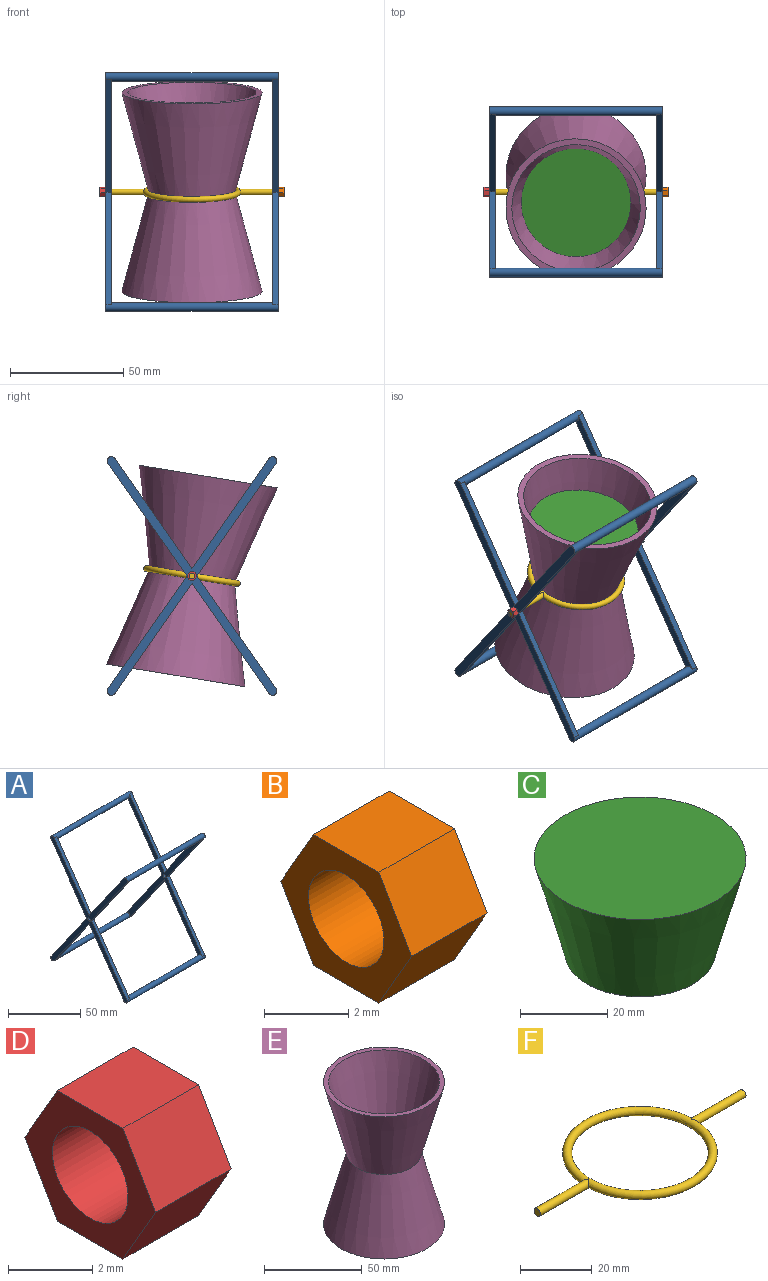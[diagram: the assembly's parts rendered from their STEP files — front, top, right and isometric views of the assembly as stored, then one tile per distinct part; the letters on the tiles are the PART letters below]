
ASSEMBLY  parts=6 mates=5
PART A: 26 faces, bbox 76.2x75x105.4 mm
  f0: cylinder r=1.91mm len=76.2mm, axis (-1,0,0), area 881.7mm2, adj f1,f11,f13,f14,f15,f16,f23,f25
  f1: plane 49.71x34.81mm, normal (0,-0.82,-0.57), area 154.1mm2, adj f0,f2,f13,f14
  f2: plane 49.71x34.81mm, normal (0,-0.82,0.57), area 154.1mm2, adj f1,f3,f13,f14
  f3: cylinder r=1.91mm len=76.2mm, axis (-1,0,0), area 881.7mm2, adj f2,f4,f13,f14,f15,f17,f18,f25
  f4: plane 48.57x34.01mm, normal (0,0.82,-0.57), area 150.6mm2, adj f3,f5,f13,f14
  f5: plane 48.57x34.01mm, normal (0,-0.82,-0.57), area 150.6mm2, adj f4,f6,f13,f14
  f6: cylinder r=1.91mm len=76.2mm, axis (-1,0,0), area 881.7mm2, adj f5,f7,f13,f14,f15,f19,f20,f25
  f7: plane 49.71x34.81mm, normal (0,0.82,0.57), area 154.1mm2, adj f6,f8,f13,f14
  f8: plane 49.71x34.81mm, normal (0,0.82,-0.57), area 154.1mm2, adj f7,f9,f13,f14
  f9: cylinder r=1.91mm len=76.2mm, axis (-1,0,0), area 881.7mm2, adj f8,f10,f13,f14,f15,f21,f22,f25
  f10: plane 48.57x34.01mm, normal (0,-0.82,0.57), area 150.6mm2, adj f9,f11,f13,f14
  f11: plane 48.57x34.01mm, normal (0,0.82,0.57), area 150.6mm2, adj f0,f10,f13,f14
  f12: cylinder r=1.27mm len=2.54mm, axis (-1,0,0), area 20.3mm2, adj f13,f14
  f13: plane 105.41x74.95mm, normal (1,0,0), area 947.4mm2, adj f0,f1,f2,f3,f4,f5,f6,f7
  f14: plane 103.79x74.26mm, normal (-1,0,0), area 901.8mm2, adj f0,f1,f2,f3,f4,f5,f6,f7
  f15: plane 103.79x74.26mm, normal (1,0,0), area 901.8mm2, adj f0,f3,f6,f9,f16,f17,f18,f19
  f16: plane 49.71x34.81mm, normal (0,-0.82,-0.57), area 154.1mm2, adj f0,f15,f17,f25
  f17: plane 49.71x34.81mm, normal (0,-0.82,0.57), area 154.1mm2, adj f3,f15,f16,f25
  f18: plane 48.57x34.01mm, normal (0,0.82,-0.57), area 150.6mm2, adj f3,f15,f19,f25
  f19: plane 48.57x34.01mm, normal (0,-0.82,-0.57), area 150.6mm2, adj f6,f15,f18,f25
  f20: plane 49.71x34.81mm, normal (0,0.82,0.57), area 154.1mm2, adj f6,f15,f21,f25
  f21: plane 49.71x34.81mm, normal (0,0.82,-0.57), area 154.1mm2, adj f9,f15,f20,f25
  f22: plane 48.57x34.01mm, normal (0,-0.82,0.57), area 150.6mm2, adj f9,f15,f23,f25
  f23: plane 48.57x34.01mm, normal (0,0.82,0.57), area 150.6mm2, adj f0,f15,f22,f25
  f24: cylinder r=1.27mm len=2.54mm, axis (1,0,0), area 20.3mm2, adj f15,f25
  f25: plane 105.41x74.95mm, normal (-1,0,0), area 947.4mm2, adj f0,f3,f6,f9,f16,f17,f18,f19
PART B: 9 faces, bbox 2.5x4.4x3.8 mm
  f0: plane 2.54x1.91mm, normal (0,0.87,0.5), area 5.6mm2, adj f1,f6,f7,f8
  f1: plane 2.54x2.2mm, normal (0,0,1), area 5.6mm2, adj f0,f2,f7,f8
  f2: plane 2.54x1.91mm, normal (0,-0.87,0.5), area 5.6mm2, adj f1,f3,f7,f8
  f3: plane 2.54x1.91mm, normal (0,-0.87,-0.5), area 5.6mm2, adj f2,f4,f7,f8
  f4: plane 2.54x2.2mm, normal (0,0,-1), area 5.6mm2, adj f3,f6,f7,f8
  f5: cylinder r=1.27mm len=2.54mm, axis (-1,0,0), area 20.3mm2, adj f7,f8
  f6: plane 2.54x1.91mm, normal (0,0.87,-0.5), area 5.6mm2, adj f0,f4,f7,f8
  f7: plane 4.4x3.81mm, normal (1,0,0), area 7.5mm2, adj f0,f1,f2,f3,f4,f5,f6
  f8: plane 4.4x3.81mm, normal (-1,0,0), area 7.5mm2, adj f0,f1,f2,f3,f4,f5,f6
PART C: 3 faces, bbox 48.6x48.6x26.7 mm
  f0: plane 48.57x48.57mm, normal (0,0,1), area 1853.1mm2, adj f1
  f1: cone r=24.29mm half-angle=15deg, axis (0,0,1), area 3600.6mm2, adj f0,f2
  f2: plane 34.25x34.25mm, normal (0,0,-1), area 921.2mm2, adj f1
PART D: 9 faces, bbox 2.5x4.4x3.8 mm
  f0: plane 2.54x1.91mm, normal (0,0.87,0.5), area 5.6mm2, adj f1,f6,f7,f8
  f1: plane 2.54x2.2mm, normal (0,0,1), area 5.6mm2, adj f0,f2,f7,f8
  f2: plane 2.54x1.91mm, normal (0,-0.87,0.5), area 5.6mm2, adj f1,f3,f7,f8
  f3: plane 2.54x1.91mm, normal (0,-0.87,-0.5), area 5.6mm2, adj f2,f4,f7,f8
  f4: plane 2.54x2.2mm, normal (0,0,-1), area 5.6mm2, adj f3,f6,f7,f8
  f5: cylinder r=1.27mm len=2.54mm, axis (1,0,0), area 20.3mm2, adj f7,f8
  f6: plane 2.54x1.91mm, normal (0,0.87,-0.5), area 5.6mm2, adj f0,f4,f7,f8
  f7: plane 4.4x3.81mm, normal (-1,0,0), area 7.5mm2, adj f0,f1,f2,f3,f4,f5,f6
  f8: plane 4.4x3.81mm, normal (1,0,0), area 7.5mm2, adj f0,f1,f2,f3,f4,f5,f6
PART E: 6 faces, bbox 61.9x61.9x88.9 mm
  f0: cone r=19.05mm half-angle=15deg, axis (0,0,-1), area 7230mm2, adj f1,f3
  f1: plane 61.92x61.92mm, normal (0,0,-1), area 489.8mm2, adj f0,f4
  f2: plane 61.92x61.92mm, normal (0,0,1), area 489.8mm2, adj f3,f5
  f3: cone r=19.05mm half-angle=15deg, axis (0,0,1), area 7230mm2, adj f0,f2
  f4: cone r=16.6mm half-angle=15deg, axis (0,0,-1), area 6469.7mm2, adj f1,f5
  f5: cone r=16.6mm half-angle=15deg, axis (0,0,1), area 6469.7mm2, adj f2,f4
PART F: 11 faces, bbox 81.3x46.8x2.5 mm
  f0: cylinder r=1.27mm len=20.28mm, axis (-1,0,0), area 155.5mm2, adj f1,f6
  f1: torus R=20.36mm, axis (0,0,1), area 1008.1mm2, adj f0,f2,f4,f5
  f2: cylinder r=1.27mm len=20.28mm, axis (1,0,0), area 155.5mm2, adj f1,f3
  f3: plane 2.54x2.54mm, normal (-1,0,0), area 5.1mm2, adj f2
  f4: cylinder r=1.27mm len=0.09mm, axis (1,0,0), area 0mm2, adj f1
  f5: cylinder r=1.27mm len=0.09mm, axis (1,0,0), area 0mm2, adj f1
  f6: plane 2.54x2.54mm, normal (1,0,0), area 5.1mm2, adj f0
  f7: torus R=20.36mm, axis (0,0,1), area 0mm2, adj f8
  f8: cylinder r=1.27mm len=0.09mm, axis (-1,0,0), area 0mm2, adj f7
  f9: torus R=20.36mm, axis (0,0,1), area 0mm2, adj f10
  f10: cylinder r=1.27mm len=0.09mm, axis (-1,0,0), area 0mm2, adj f9
PLACE A t=(-0.25,0.04,0.47)mm fixed
PLACE B rot(axis=(1,0,0),9.3deg) t=(-0.25,0.04,0.47)mm
PLACE C rot(axis=(1,0,0),9.3deg) t=(-0.25,0.05,0.39)mm
PLACE D rot(axis=(1,0,0),9.3deg) t=(-0.25,0.04,0.47)mm
PLACE E rot(axis=(1,0,0),9.3deg) t=(-0.25,0.04,0.47)mm
PLACE F rot(axis=(1,0,0),9.3deg) t=(-0.25,0.04,0.47)mm
MATE fastened B.f5 <-> F.f0  axis (1,0,0) through (40.39,0.04,0.47)mm
MATE fastened C.f1 <-> E.f0  axis (0,0.16,-0.99) through (-0.25,-0.37,2.98)mm
MATE revolute F.f0 <-> A.f12  axis (1,0,0) through (40.39,0.04,0.47)mm
MATE fastened F.f1 <-> E.f0  axis (0,-0.16,0.99) through (-0.25,0.04,0.47)mm
MATE fastened D.f5 <-> F.f0  axis (-1,0,0) through (-40.89,0.04,0.47)mm
